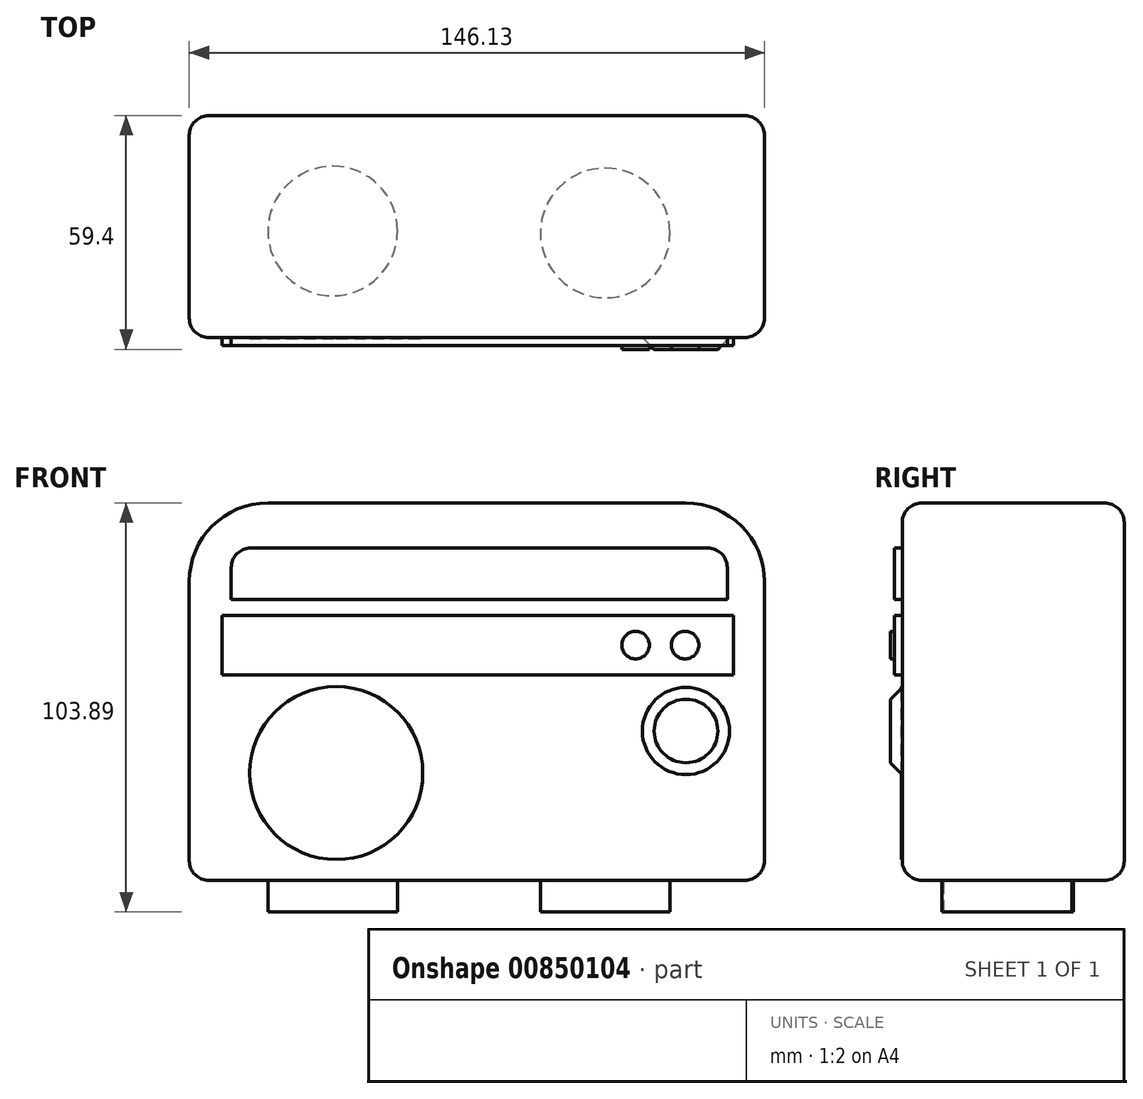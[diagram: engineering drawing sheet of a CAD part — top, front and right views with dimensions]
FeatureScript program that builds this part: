
annotation { "Feature Type Name" : "Feature", "Feature Type Description" : "" }
export const myFeature = defineFeature(function(context is Context, id is Id, definition is map)
    precondition{}
    {
        {
            var Q0;
            Q0=qCreatedBy(makeId("Front.planeOp"),FACE);
            var sketch = newSketch(context, id + "F0", { "sketchPlane" : qUnion([Q0])});
            skLineSegment(sketch, "E0.bottom", {"start": v(-53.18, 52.36) * mm, "end": v(52.95, 52.36) * mm});
            skLineSegment(sketch, "E0.top", {"start": v(-73.18, -43.53) * mm, "end": v(72.95, -43.53) * mm});
            skLineSegment(sketch, "E0.left", {"start": v(-73.18, 32.36) * mm, "end": v(-73.18, -43.53) * mm});
            skLineSegment(sketch, "E0.right", {"start": v(72.95, 32.36) * mm, "end": v(72.95, -43.53) * mm});
            skPoint(sketch, "E1.visualSharp", {"position": v(-73.18, 52.36) * mm});
            skArc(sketch, "E1.filletArc", {"start": v(-53.18, 52.36) * mm, "mid": v(-67.32, 46.5) * mm, "end": v(-73.18, 32.36) * mm});
            skPoint(sketch, "E2.visualSharp", {"position": v(72.95, 52.36) * mm});
            skArc(sketch, "E2.filletArc", {"start": v(72.95, 32.36) * mm, "mid": v(67.09, 46.5) * mm, "end": v(52.95, 52.36) * mm});
            skSolve(sketch);
        }
        {
            var Q0;
            Q0=makeQuery(id+"F0.imprint","IMPRINT",FACE,{"disambiguationData":[TD([[makeQuery(id+"F0.imprint","IMPRINT",EDGE,{"derivedFrom":sQuery(id+"F0.wireOp",EDGE,"E0.bottom")}),-1.0]])]});
            extrude(context, id + "F1", {"entities" : qUnion([Q0]), "oppositeDirection" : true, "depth" : 56.4 * mm, "offsetDistance" : 25 * mm});
        }
        {
            var Q0;
            Q0=makeQuery(id+"F1.opExtrude","SWEPT_FACE",FACE,{"disambiguationData":[OSD([sQuery(id+"F0.wireOp",EDGE,"E0.top")])]});
            var sketch = newSketch(context, id + "F2", { "sketchPlane" : qUnion([Q0])});
            skCircle(sketch, "E3", {"center": v(-36.72, -27.08) * mm, "radius": 16.47 * mm});
            skCircle(sketch, "E4", {"center": v(32.5, -26.61) * mm, "radius": 16.47 * mm});
            skSolve(sketch);
        }
        {
            var Q0;
            Q0=makeQuery(id+"F1.opExtrude","CAP_FACE",FACE,{"disambiguationData":[OSD([sQuery(id+"F0.wireOp",EDGE,"E0.bottom"),sQuery(id+"F0.wireOp",EDGE,"E0.top"),sQuery(id+"F0.wireOp",EDGE,"E0.left"),sQuery(id+"F0.wireOp",EDGE,"E0.right"),sQuery(id+"F0.wireOp",EDGE,"E1.filletArc"),sQuery(id+"F0.wireOp",EDGE,"E2.filletArc")])],"isStart":true});
            var sketch = newSketch(context, id + "F3", { "sketchPlane" : qUnion([Q0])});
            skCircle(sketch, "E5", {"center": v(53.01, -5.58) * mm, "radius": 13.08 * mm});
            skPoint(sketch, "E5.centerSnap0", {"position": v(72.95, -5.58) * mm});
            skSolve(sketch);
        }
        {
            var Q0;
            Q0=makeQuery(id+"F1.opExtrude","CAP_FACE",FACE,{"disambiguationData":[OSD([sQuery(id+"F0.wireOp",EDGE,"E0.bottom"),sQuery(id+"F0.wireOp",EDGE,"E0.top"),sQuery(id+"F0.wireOp",EDGE,"E0.left"),sQuery(id+"F0.wireOp",EDGE,"E0.right"),sQuery(id+"F0.wireOp",EDGE,"E1.filletArc"),sQuery(id+"F0.wireOp",EDGE,"E2.filletArc")])],"isStart":true});
            var sketch = newSketch(context, id + "F4", { "sketchPlane" : qUnion([Q0])});
            skLineSegment(sketch, "E6.bottom", {"start": v(-64.87, 23.84) * mm, "end": v(65.11, 23.84) * mm});
            skLineSegment(sketch, "E6.top", {"start": v(-64.87, 8.66) * mm, "end": v(65.11, 8.66) * mm});
            skLineSegment(sketch, "E6.left", {"start": v(-64.87, 23.84) * mm, "end": v(-64.87, 8.66) * mm});
            skLineSegment(sketch, "E6.right", {"start": v(65.11, 23.84) * mm, "end": v(65.11, 8.66) * mm});
            skSolve(sketch);
        }
        {
            var Q0;
            Q0 = qSketchRegion(id + "F4", true);
            extrude(context, id + "F5", {"entities" : qUnion([Q0]), "depth" : 2 * mm, "offsetDistance" : 25 * mm});
        }
        {
            var Q0;
            Q0=makeQuery(id+"F5.opExtrude","CAP_FACE",FACE,{"disambiguationData":[OSD([sQuery(id+"F4.wireOp",EDGE,"E6.bottom"),sQuery(id+"F4.wireOp",EDGE,"E6.top"),sQuery(id+"F4.wireOp",EDGE,"E6.left"),sQuery(id+"F4.wireOp",EDGE,"E6.right")])],"isStart":false});
            var sketch = newSketch(context, id + "F6", { "sketchPlane" : qUnion([Q0])});
            skCircle(sketch, "E7", {"center": v(52.78, 16.25) * mm, "radius": 3.5 * mm});
            skCircle(sketch, "E8", {"center": v(40.2, 16.25) * mm, "radius": 3.5 * mm});
            skSolve(sketch);
        }
        {
            var Q0;
            Q0 = qSketchRegion(id + "F6", true);
            extrude(context, id + "F7", {"entities" : qUnion([Q0]), "depth" : 1 * mm, "offsetDistance" : 25 * mm});
        }
        {
            var Q0;
            Q0=makeQuery(id+"F2.imprint","IMPRINT",FACE,{"disambiguationData":[TD([[makeQuery(id+"F2.imprint","IMPRINT",EDGE,{"derivedFrom":sQuery(id+"F2.wireOp",EDGE,"E3")}),1.0]])]});
            var Q1;
            Q1=makeQuery(id+"F2.imprint","IMPRINT",FACE,{"disambiguationData":[TD([[makeQuery(id+"F2.imprint","IMPRINT",EDGE,{"derivedFrom":sQuery(id+"F2.wireOp",EDGE,"E4")}),1.0]])]});
            extrude(context, id + "F8", {"entities" : qUnion([Q0, Q1]), "depth" : 8 * mm, "offsetDistance" : 25 * mm});
        }
        {
            var Q0;
            Q0=makeQuery(id+"F3.imprint","IMPRINT",FACE,{"disambiguationData":[TD([[makeQuery(id+"F3.imprint","IMPRINT",EDGE,{"derivedFrom":sQuery(id+"F3.wireOp",EDGE,"E5")}),1.0]])]});
            extrude(context, id + "F9", {"entities" : qUnion([Q0]), "depth" : 3 * mm, "offsetDistance" : 25 * mm});
        }
        {
            var Q0;
            Q0=makeQuery(id+"F1.opExtrude","CAP_FACE",FACE,{"disambiguationData":[OSD([sQuery(id+"F0.wireOp",EDGE,"E0.bottom"),sQuery(id+"F0.wireOp",EDGE,"E0.top"),sQuery(id+"F0.wireOp",EDGE,"E0.left"),sQuery(id+"F0.wireOp",EDGE,"E0.right"),sQuery(id+"F0.wireOp",EDGE,"E1.filletArc"),sQuery(id+"F0.wireOp",EDGE,"E2.filletArc")])],"isStart":true});
            var sketch = newSketch(context, id + "F10", { "sketchPlane" : qUnion([Q0])});
            skLineSegment(sketch, "E9.bottom", {"start": v(-57.5, 40.94) * mm, "end": v(58.5, 40.94) * mm});
            skLineSegment(sketch, "E9.top", {"start": v(-62.5, 27.87) * mm, "end": v(63.5, 27.87) * mm});
            skLineSegment(sketch, "E9.left", {"start": v(-62.5, 35.94) * mm, "end": v(-62.5, 27.87) * mm});
            skLineSegment(sketch, "E9.right", {"start": v(63.5, 35.94) * mm, "end": v(63.5, 27.87) * mm});
            skPoint(sketch, "E10.visualSharp", {"position": v(-62.5, 40.94) * mm});
            skArc(sketch, "E10.filletArc", {"start": v(-57.5, 40.94) * mm, "mid": v(-61.04, 39.47) * mm, "end": v(-62.5, 35.94) * mm});
            skPoint(sketch, "E11.visualSharp", {"position": v(63.5, 40.94) * mm});
            skArc(sketch, "E11.filletArc", {"start": v(63.5, 35.94) * mm, "mid": v(62.03, 39.47) * mm, "end": v(58.5, 40.94) * mm});
            skSolve(sketch);
        }
        {
            var Q0;
            Q0=makeQuery(id+"F10.imprint","IMPRINT",FACE,{"disambiguationData":[TD([[makeQuery(id+"F10.imprint","IMPRINT",EDGE,{"derivedFrom":sQuery(id+"F10.wireOp",EDGE,"E9.bottom")}),-1.0]])]});
            extrude(context, id + "F11", {"entities" : qUnion([Q0]), "depth" : 2 * mm, "offsetDistance" : 25 * mm});
        }
        {
            var Q0;
            Q0=makeQuery(id+"F11.opExtrude","CAP_FACE",FACE,{"disambiguationData":[OSD([sQuery(id+"F10.wireOp",EDGE,"E9.bottom"),sQuery(id+"F10.wireOp",EDGE,"E9.top"),sQuery(id+"F10.wireOp",EDGE,"E9.left"),sQuery(id+"F10.wireOp",EDGE,"E9.right"),sQuery(id+"F10.wireOp",EDGE,"E10.filletArc"),sQuery(id+"F10.wireOp",EDGE,"E11.filletArc")])],"isStart":false});
            var sketch = newSketch(context, id + "F12", { "sketchPlane" : qUnion([Q0])});
            skLineSegment(sketch, "E12", {"start": v(-57.5, 35.94) * mm, "end": v(43.5, 35.94) * mm});
            skLineSegment(sketch, "E13", {"start": v(-56.15, 34.22) * mm, "end": v(44.85, 34.22) * mm});
            skSolve(sketch);
        }
        {
            var Q0;
            Q0=sQuery(id+"F12.wireOp",EDGE,"E13");
            var Q1;
            Q1=sQuery(id+"F12.wireOp",EDGE,"E12");
            extrude(context, id + "F13", {"bodyType" : ToolBodyType.SURFACE, "surfaceEntities" : qUnion([Q0, Q1]), "depth" : 1 * mm, "offsetDistance" : 25 * mm});
        }
        {
            var Q0;
            Q0=makeQuery(id+"F11.opExtrude","CAP_FACE",FACE,{"disambiguationData":[OSD([sQuery(id+"F10.wireOp",EDGE,"E9.bottom"),sQuery(id+"F10.wireOp",EDGE,"E9.top"),sQuery(id+"F10.wireOp",EDGE,"E9.left"),sQuery(id+"F10.wireOp",EDGE,"E9.right"),sQuery(id+"F10.wireOp",EDGE,"E10.filletArc"),sQuery(id+"F10.wireOp",EDGE,"E11.filletArc")])],"isStart":false});
            var sketch = newSketch(context, id + "F14", { "sketchPlane" : qUnion([Q0])});
            skLineSegment(sketch, "E14", {"start": v(-55.64, 31.84) * mm, "end": v(44.36, 31.84) * mm});
            skSolve(sketch);
        }
        {
            var Q0;
            Q0=sQuery(id+"F14.wireOp",EDGE,"E14");
            extrude(context, id + "F15", {"bodyType" : ToolBodyType.SURFACE, "surfaceEntities" : qUnion([Q0]), "depth" : 1 * mm, "offsetDistance" : 25 * mm});
        }
        {
            var Q0;
            Q0=makeQuery(id+"F15.opExtrude","SWEPT_BODY",BODY,{"disambiguationData":[OSD([sQuery(id+"F14.wireOp",EDGE,"E14")])]});
            var Q1;
            Q1=makeQuery(id+"F13.opExtrude","SWEPT_BODY",BODY,{"disambiguationData":[OSD([sQuery(id+"F12.wireOp",EDGE,"E13")])]});
            var Q2;
            Q2=makeQuery(id+"F13.opExtrude","SWEPT_BODY",BODY,{"disambiguationData":[OSD([sQuery(id+"F12.wireOp",EDGE,"E12")])]});
            deleteBodies(context, id + "F16", {"entities" : qUnion([Q0, Q1, Q2])});
        }
        {
            var Q0;
            Q0=makeQuery(id+"F11.opExtrude","CAP_FACE",FACE,{"disambiguationData":[OSD([sQuery(id+"F10.wireOp",EDGE,"E9.bottom"),sQuery(id+"F10.wireOp",EDGE,"E9.top"),sQuery(id+"F10.wireOp",EDGE,"E9.left"),sQuery(id+"F10.wireOp",EDGE,"E9.right"),sQuery(id+"F10.wireOp",EDGE,"E10.filletArc"),sQuery(id+"F10.wireOp",EDGE,"E11.filletArc")])],"isStart":false});
            var sketch = newSketch(context, id + "F17", { "sketchPlane" : qUnion([Q0])});
            skLineSegment(sketch, "E15", {"start": v(-57.5, 35.94) * mm, "end": v(43.64, 35.94) * mm});
            skSolve(sketch);
        }
        {
            var Q0;
            Q0=sQuery(id+"F17.wireOp",EDGE,"E15");
            extrude(context, id + "F18", {"bodyType" : ToolBodyType.SURFACE, "surfaceEntities" : qUnion([Q0]), "depth" : 1 * mm, "offsetDistance" : 25 * mm});
        }
        {
            var Q0;
            Q0=makeQuery(id+"F11.opExtrude","CAP_FACE",FACE,{"disambiguationData":[OSD([sQuery(id+"F10.wireOp",EDGE,"E9.bottom"),sQuery(id+"F10.wireOp",EDGE,"E9.top"),sQuery(id+"F10.wireOp",EDGE,"E9.left"),sQuery(id+"F10.wireOp",EDGE,"E9.right"),sQuery(id+"F10.wireOp",EDGE,"E10.filletArc"),sQuery(id+"F10.wireOp",EDGE,"E11.filletArc")])],"isStart":false});
            var sketch = newSketch(context, id + "F19", { "sketchPlane" : qUnion([Q0])});
            skLineSegment(sketch, "E16", {"start": v(-56.14, 35.4) * mm, "end": v(43.86, 35.4) * mm});
            skSolve(sketch);
        }
        {
            var Q0;
            Q0=sQuery(id+"F19.wireOp",EDGE,"E16");
            extrude(context, id + "F20", {"bodyType" : ToolBodyType.SURFACE, "surfaceEntities" : qUnion([Q0]), "depth" : 1 * mm, "offsetDistance" : 25 * mm});
        }
        {
            var Q0;
            Q0=makeQuery(id+"F11.opExtrude","CAP_FACE",FACE,{"disambiguationData":[OSD([sQuery(id+"F10.wireOp",EDGE,"E9.bottom"),sQuery(id+"F10.wireOp",EDGE,"E9.top"),sQuery(id+"F10.wireOp",EDGE,"E9.left"),sQuery(id+"F10.wireOp",EDGE,"E9.right"),sQuery(id+"F10.wireOp",EDGE,"E10.filletArc"),sQuery(id+"F10.wireOp",EDGE,"E11.filletArc")])],"isStart":false});
            var sketch = newSketch(context, id + "F21", { "sketchPlane" : qUnion([Q0])});
            skLineSegment(sketch, "E17", {"start": v(-57.5, 33.3) * mm, "end": v(42.5, 33.3) * mm});
            skSolve(sketch);
        }
        {
            var Q0;
            Q0=sQuery(id+"F21.wireOp",EDGE,"E17");
            extrude(context, id + "F22", {"bodyType" : ToolBodyType.SURFACE, "surfaceEntities" : qUnion([Q0]), "depth" : 1 * mm, "offsetDistance" : 25 * mm});
        }
        {
            var Q0;
            Q0=makeQuery(id+"F11.opExtrude","CAP_FACE",FACE,{"disambiguationData":[OSD([sQuery(id+"F10.wireOp",EDGE,"E9.bottom"),sQuery(id+"F10.wireOp",EDGE,"E9.top"),sQuery(id+"F10.wireOp",EDGE,"E9.left"),sQuery(id+"F10.wireOp",EDGE,"E9.right"),sQuery(id+"F10.wireOp",EDGE,"E10.filletArc"),sQuery(id+"F10.wireOp",EDGE,"E11.filletArc")])],"isStart":false});
            var sketch = newSketch(context, id + "F23", { "sketchPlane" : qUnion([Q0])});
            skLineSegment(sketch, "E18", {"start": v(-56.14, 31.84) * mm, "end": v(44.23, 31.84) * mm});
            skSolve(sketch);
        }
        {
            var Q0;
            Q0=sQuery(id+"F23.wireOp",EDGE,"E18");
            extrude(context, id + "F24", {"bodyType" : ToolBodyType.SURFACE, "surfaceEntities" : qUnion([Q0]), "depth" : 1 * mm, "offsetDistance" : 25 * mm});
        }
        {
            var Q0;
            Q0=makeQuery(id+"F11.opExtrude","CAP_FACE",FACE,{"disambiguationData":[OSD([sQuery(id+"F10.wireOp",EDGE,"E9.bottom"),sQuery(id+"F10.wireOp",EDGE,"E9.top"),sQuery(id+"F10.wireOp",EDGE,"E9.left"),sQuery(id+"F10.wireOp",EDGE,"E9.right"),sQuery(id+"F10.wireOp",EDGE,"E10.filletArc"),sQuery(id+"F10.wireOp",EDGE,"E11.filletArc")])],"isStart":false});
            var sketch = newSketch(context, id + "F25", { "sketchPlane" : qUnion([Q0])});
            skLineSegment(sketch, "E19", {"start": v(-56.14, 30.25) * mm, "end": v(43.86, 30.25) * mm});
            skSolve(sketch);
        }
        {
            var Q0;
            Q0=sQuery(id+"F25.wireOp",EDGE,"E19");
            extrude(context, id + "F26", {"bodyType" : ToolBodyType.SURFACE, "surfaceEntities" : qUnion([Q0]), "depth" : 1 * mm, "offsetDistance" : 25 * mm});
        }
        {
            var Q0;
            Q0=makeQuery(id+"F11.opExtrude","CAP_FACE",FACE,{"disambiguationData":[OSD([sQuery(id+"F10.wireOp",EDGE,"E9.bottom"),sQuery(id+"F10.wireOp",EDGE,"E9.top"),sQuery(id+"F10.wireOp",EDGE,"E9.left"),sQuery(id+"F10.wireOp",EDGE,"E9.right"),sQuery(id+"F10.wireOp",EDGE,"E10.filletArc"),sQuery(id+"F10.wireOp",EDGE,"E11.filletArc")])],"isStart":false});
            var sketch = newSketch(context, id + "F27", { "sketchPlane" : qUnion([Q0])});
            skLineSegment(sketch, "E20", {"start": v(-55.94, 39.18) * mm, "end": v(44.06, 39.18) * mm});
            skSolve(sketch);
        }
        {
            var Q0;
            Q0=sQuery(id+"F27.wireOp",EDGE,"E20");
            extrude(context, id + "F28", {"bodyType" : ToolBodyType.SURFACE, "surfaceEntities" : qUnion([Q0]), "depth" : 1 * mm, "offsetDistance" : 25 * mm});
        }
        {
            var Q0;
            Q0=makeQuery(id+"F9.opExtrude","CAP_FACE",FACE,{"disambiguationData":[OSD([sQuery(id+"F3.wireOp",EDGE,"E5")])],"isStart":false});
            chamfer(context, id + "F29", {"entities" : qUnion([Q0]), "width" : 5 * mm, "tangentPropagation" : true});
        }
        {
            var Q0;
            Q0=makeQuery(id+"F11.opExtrude","CAP_FACE",FACE,{"disambiguationData":[OSD([sQuery(id+"F10.wireOp",EDGE,"E9.bottom"),sQuery(id+"F10.wireOp",EDGE,"E9.top"),sQuery(id+"F10.wireOp",EDGE,"E9.left"),sQuery(id+"F10.wireOp",EDGE,"E9.right"),sQuery(id+"F10.wireOp",EDGE,"E10.filletArc"),sQuery(id+"F10.wireOp",EDGE,"E11.filletArc")])],"isStart":false});
            var sketch = newSketch(context, id + "F30", { "sketchPlane" : qUnion([Q0])});
            skLineSegment(sketch, "E21", {"start": v(43.64, 40.94) * mm, "end": v(43.64, 27.87) * mm});
            skSolve(sketch);
        }
        {
            var Q0;
            Q0=sQuery(id+"F30.wireOp",EDGE,"E21");
            extrude(context, id + "F31", {"bodyType" : ToolBodyType.SURFACE, "surfaceEntities" : qUnion([Q0]), "depth" : 1 * mm, "offsetDistance" : 25 * mm});
        }
        {
            var Q0;
            Q0=makeQuery(id+"F11.opExtrude","CAP_FACE",FACE,{"disambiguationData":[OSD([sQuery(id+"F10.wireOp",EDGE,"E9.bottom"),sQuery(id+"F10.wireOp",EDGE,"E9.top"),sQuery(id+"F10.wireOp",EDGE,"E9.left"),sQuery(id+"F10.wireOp",EDGE,"E9.right"),sQuery(id+"F10.wireOp",EDGE,"E10.filletArc"),sQuery(id+"F10.wireOp",EDGE,"E11.filletArc")])],"isStart":false});
            var sketch = newSketch(context, id + "F32", { "sketchPlane" : qUnion([Q0])});
            skLineSegment(sketch, "E22", {"start": v(-57.5, 40.94) * mm, "end": v(-57.5, 27.87) * mm});
            skSolve(sketch);
        }
        {
            var Q0;
            Q0=sQuery(id+"F32.wireOp",EDGE,"E22");
            extrude(context, id + "F33", {"bodyType" : ToolBodyType.SURFACE, "surfaceEntities" : qUnion([Q0]), "depth" : 1 * mm, "offsetDistance" : 25 * mm});
        }
        {
            var Q0;
            Q0=makeQuery(id+"F1.opExtrude","CAP_FACE",FACE,{"disambiguationData":[OSD([sQuery(id+"F0.wireOp",EDGE,"E0.bottom"),sQuery(id+"F0.wireOp",EDGE,"E0.top"),sQuery(id+"F0.wireOp",EDGE,"E0.left"),sQuery(id+"F0.wireOp",EDGE,"E0.right"),sQuery(id+"F0.wireOp",EDGE,"E1.filletArc"),sQuery(id+"F0.wireOp",EDGE,"E2.filletArc")])],"isStart":true});
            fillet(context, id + "F34", {"entities" : qUnion([Q0]), "radius" : 5 * mm, "tangentPropagation" : true, "allowEdgeOverflow" : false});
        }
        {
            var Q0;
            Q0=makeQuery(id+"F1.opExtrude","CAP_FACE",FACE,{"disambiguationData":[OSD([sQuery(id+"F0.wireOp",EDGE,"E0.bottom"),sQuery(id+"F0.wireOp",EDGE,"E0.top"),sQuery(id+"F0.wireOp",EDGE,"E0.left"),sQuery(id+"F0.wireOp",EDGE,"E0.right"),sQuery(id+"F0.wireOp",EDGE,"E1.filletArc"),sQuery(id+"F0.wireOp",EDGE,"E2.filletArc")])],"isStart":false});
            fillet(context, id + "F35", {"entities" : qUnion([Q0]), "radius" : 5 * mm, "tangentPropagation" : true, "allowEdgeOverflow" : false});
        }
        {
            var Q0;
            Q0=makeQuery(id+"F1.opExtrude","SWEPT_FACE",FACE,{"disambiguationData":[OSD([sQuery(id+"F0.wireOp",EDGE,"E0.right")])]});
            fillet(context, id + "F36", {"entities" : qUnion([Q0]), "radius" : 5 * mm, "tangentPropagation" : true, "allowEdgeOverflow" : false});
        }
        {
            var Q0;
            Q0=makeQuery(id+"F1.opExtrude","SWEPT_FACE",FACE,{"disambiguationData":[OSD([sQuery(id+"F0.wireOp",EDGE,"E0.left")])]});
            fillet(context, id + "F37", {"entities" : qUnion([Q0]), "radius" : 5 * mm, "tangentPropagation" : true, "allowEdgeOverflow" : false});
        }
        {
            var Q0;
            Q0=makeQuery(id+"F18.opExtrude","SWEPT_BODY",BODY,{"disambiguationData":[OSD([sQuery(id+"F17.wireOp",EDGE,"E15")])]});
            var Q1;
            Q1=makeQuery(id+"F28.opExtrude","SWEPT_BODY",BODY,{"disambiguationData":[OSD([sQuery(id+"F27.wireOp",EDGE,"E20")])]});
            var Q2;
            Q2=makeQuery(id+"F22.opExtrude","SWEPT_BODY",BODY,{"disambiguationData":[OSD([sQuery(id+"F21.wireOp",EDGE,"E17")])]});
            var Q3;
            Q3=makeQuery(id+"F26.opExtrude","SWEPT_BODY",BODY,{"disambiguationData":[OSD([sQuery(id+"F25.wireOp",EDGE,"E19")])]});
            var Q4;
            Q4=makeQuery(id+"F24.opExtrude","SWEPT_BODY",BODY,{"disambiguationData":[OSD([sQuery(id+"F23.wireOp",EDGE,"E18")])]});
            deleteBodies(context, id + "F38", {"entities" : qUnion([Q0, Q1, Q2, Q3, Q4])});
        }
        {
            var Q0;
            Q0=makeQuery(id+"F20.opExtrude","SWEPT_BODY",BODY,{"disambiguationData":[OSD([sQuery(id+"F19.wireOp",EDGE,"E16")])]});
            deleteBodies(context, id + "F39", {"entities" : qUnion([Q0])});
        }
        {
            var Q0;
            Q0=makeQuery(id+"F1.opExtrude","CAP_FACE",FACE,{"disambiguationData":[OSD([sQuery(id+"F0.wireOp",EDGE,"E0.bottom"),sQuery(id+"F0.wireOp",EDGE,"E0.top"),sQuery(id+"F0.wireOp",EDGE,"E0.left"),sQuery(id+"F0.wireOp",EDGE,"E0.right"),sQuery(id+"F0.wireOp",EDGE,"E1.filletArc"),sQuery(id+"F0.wireOp",EDGE,"E2.filletArc")])],"isStart":true});
            var sketch = newSketch(context, id + "F40", { "sketchPlane" : qUnion([Q0])});
            skCircle(sketch, "E23", {"center": v(-35.84, -16.26) * mm, "radius": 22 * mm});
            skSolve(sketch);
        }
        {
            var Q0;
            Q0=makeQuery(id+"F40.imprint","IMPRINT",FACE,{"disambiguationData":[TD([[makeQuery(id+"F40.imprint","IMPRINT",EDGE,{"derivedFrom":sQuery(id+"F40.wireOp",EDGE,"E23")}),1.0]])]});
            extrude(context, id + "F41", {"entities" : qUnion([Q0]), "depth" : 0.2 * mm, "offsetDistance" : 25 * mm});
        }
        {
            var Q0;
            Q0=makeQuery(id+"F41.opExtrude","CAP_FACE",FACE,{"disambiguationData":[OSD([sQuery(id+"F40.wireOp",EDGE,"E23")])],"isStart":false});
            var sketch = newSketch(context, id + "F42", { "sketchPlane" : qUnion([Q0])});
            skLineSegment(sketch, "E24", {"start": v(-50.66, 0) * mm, "end": v(-21.02, 0) * mm});
            skLineSegment(sketch, "E25", {"start": v(-52.31, -1.68) * mm, "end": v(-19.37, -1.68) * mm});
            skLineSegment(sketch, "E26", {"start": v(-53.38, -2.99) * mm, "end": v(-18.3, -2.99) * mm});
            skLineSegment(sketch, "E27", {"start": v(-54.36, -4.39) * mm, "end": v(-17.32, -4.39) * mm});
            skLineSegment(sketch, "E28", {"start": v(-54.87, -5.23) * mm, "end": v(-16.8, -5.23) * mm});
            skLineSegment(sketch, "E29", {"start": v(-55.58, -6.55) * mm, "end": v(-16.1, -6.55) * mm});
            skLineSegment(sketch, "E30", {"start": v(-56.12, -7.74) * mm, "end": v(-15.56, -7.74) * mm});
            skLineSegment(sketch, "E31", {"start": v(-51.49, -0.8) * mm, "end": v(-20.2, -0.8) * mm});
            skLineSegment(sketch, "E32", {"start": v(-56.58, -8.92) * mm, "end": v(-15.1, -8.92) * mm});
            skLineSegment(sketch, "E33", {"start": v(-56.98, -10.18) * mm, "end": v(-14.7, -10.18) * mm});
            skLineSegment(sketch, "E34", {"start": v(-57.27, -11.27) * mm, "end": v(-14.42, -11.27) * mm});
            skLineSegment(sketch, "E35", {"start": v(-57.5, -12.41) * mm, "end": v(-14.18, -12.41) * mm});
            skLineSegment(sketch, "E36", {"start": v(-57.66, -13.44) * mm, "end": v(-14.03, -13.44) * mm});
            skLineSegment(sketch, "E37", {"start": v(-57.77, -14.46) * mm, "end": v(-13.92, -14.46) * mm});
            skLineSegment(sketch, "E38", {"start": v(-57.83, -15.54) * mm, "end": v(-13.86, -15.54) * mm});
            skLineSegment(sketch, "E39", {"start": v(-57.84, -16.53) * mm, "end": v(-13.85, -16.53) * mm});
            skLineSegment(sketch, "E40", {"start": v(-57.8, -17.6) * mm, "end": v(-13.89, -17.6) * mm});
            skLineSegment(sketch, "E41", {"start": v(-57.73, -18.46) * mm, "end": v(-13.96, -18.46) * mm});
            skLineSegment(sketch, "E42", {"start": v(-57.59, -19.57) * mm, "end": v(-14.1, -19.57) * mm});
            skLineSegment(sketch, "E43", {"start": v(-57.39, -20.7) * mm, "end": v(-14.3, -20.7) * mm});
            skLineSegment(sketch, "E44", {"start": v(-57.16, -21.67) * mm, "end": v(-14.52, -21.67) * mm});
            skLineSegment(sketch, "E45", {"start": v(-56.94, -22.47) * mm, "end": v(-14.74, -22.47) * mm});
            skLineSegment(sketch, "E46", {"start": v(-56.65, -23.4) * mm, "end": v(-15.04, -23.4) * mm});
            skLineSegment(sketch, "E47", {"start": v(-56.27, -24.42) * mm, "end": v(-15.41, -24.42) * mm});
            skLineSegment(sketch, "E48", {"start": v(-55.87, -25.35) * mm, "end": v(-15.81, -25.35) * mm});
            skLineSegment(sketch, "E49", {"start": v(-55.31, -26.5) * mm, "end": v(-16.37, -26.5) * mm});
            skLineSegment(sketch, "E50", {"start": v(-54.73, -27.53) * mm, "end": v(-16.95, -27.53) * mm});
            skLineSegment(sketch, "E51", {"start": v(-54.3, -28.22) * mm, "end": v(-17.38, -28.22) * mm});
            skLineSegment(sketch, "E52", {"start": v(-53.66, -29.16) * mm, "end": v(-18.02, -29.16) * mm});
            skLineSegment(sketch, "E53", {"start": v(-52.8, -30.26) * mm, "end": v(-18.87, -30.26) * mm});
            skLineSegment(sketch, "E54", {"start": v(-52.04, -31.15) * mm, "end": v(-19.65, -31.15) * mm});
            skLineSegment(sketch, "E55", {"start": v(-51.3, -31.91) * mm, "end": v(-20.39, -31.91) * mm});
            skLineSegment(sketch, "E56", {"start": v(-50.38, -32.76) * mm, "end": v(-21.3, -32.76) * mm});
            skLineSegment(sketch, "E57", {"start": v(-49.41, -33.57) * mm, "end": v(-22.27, -33.57) * mm});
            skLineSegment(sketch, "E58", {"start": v(-48.63, -34.16) * mm, "end": v(-23.05, -34.16) * mm});
            skLineSegment(sketch, "E59", {"start": v(-47.54, -34.89) * mm, "end": v(-24.14, -34.89) * mm});
            skLineSegment(sketch, "E60", {"start": v(-46.14, -35.7) * mm, "end": v(-25.54, -35.7) * mm});
            skLineSegment(sketch, "E61", {"start": v(-43.41, -36.91) * mm, "end": v(-27.31, -36.53) * mm});
            skLineSegment(sketch, "E62", {"start": v(-40.68, -37.72) * mm, "end": v(-31, -37.72) * mm});
            skLineSegment(sketch, "E63", {"start": v(-49.69, 0.83) * mm, "end": v(-22, 0.83) * mm});
            skLineSegment(sketch, "E64", {"start": v(-48.31, 1.86) * mm, "end": v(-23.37, 1.86) * mm});
            skLineSegment(sketch, "E65", {"start": v(-46.57, 2.94) * mm, "end": v(-25.11, 2.94) * mm});
            skLineSegment(sketch, "E66", {"start": v(-44.42, 4) * mm, "end": v(-27.26, 4) * mm});
            skLineSegment(sketch, "E67", {"start": v(-41.86, 4.9) * mm, "end": v(-29.82, 4.9) * mm});
            skSolve(sketch);
        }
        {
            var Q0;
            Q0=sQuery(id+"F42.wireOp",EDGE,"E67");
            var Q1;
            Q1=sQuery(id+"F42.wireOp",EDGE,"E66");
            var Q2;
            Q2=sQuery(id+"F42.wireOp",EDGE,"E65");
            var Q3;
            Q3=sQuery(id+"F42.wireOp",EDGE,"E64");
            var Q4;
            Q4=sQuery(id+"F42.wireOp",EDGE,"E63");
            var Q5;
            Q5=sQuery(id+"F42.wireOp",EDGE,"E24");
            var Q6;
            Q6=sQuery(id+"F42.wireOp",EDGE,"E31");
            var Q7;
            Q7=sQuery(id+"F42.wireOp",EDGE,"E25");
            var Q8;
            Q8=sQuery(id+"F42.wireOp",EDGE,"E26");
            var Q9;
            Q9=sQuery(id+"F42.wireOp",EDGE,"E27");
            var Q10;
            Q10=sQuery(id+"F42.wireOp",EDGE,"E28");
            var Q11;
            Q11=sQuery(id+"F42.wireOp",EDGE,"E29");
            var Q12;
            Q12=sQuery(id+"F42.wireOp",EDGE,"E30");
            var Q13;
            Q13=sQuery(id+"F42.wireOp",EDGE,"E32");
            var Q14;
            Q14=sQuery(id+"F42.wireOp",EDGE,"E33");
            var Q15;
            Q15=sQuery(id+"F42.wireOp",EDGE,"E34");
            var Q16;
            Q16=sQuery(id+"F42.wireOp",EDGE,"E35");
            var Q17;
            Q17=sQuery(id+"F42.wireOp",EDGE,"E36");
            var Q18;
            Q18=sQuery(id+"F42.wireOp",EDGE,"E37");
            var Q19;
            Q19=sQuery(id+"F42.wireOp",EDGE,"E38");
            var Q20;
            Q20=sQuery(id+"F42.wireOp",EDGE,"E39");
            var Q21;
            Q21=sQuery(id+"F42.wireOp",EDGE,"E40");
            var Q22;
            Q22=sQuery(id+"F42.wireOp",EDGE,"E41");
            var Q23;
            Q23=sQuery(id+"F42.wireOp",EDGE,"E42");
            var Q24;
            Q24=sQuery(id+"F42.wireOp",EDGE,"E43");
            var Q25;
            Q25=sQuery(id+"F42.wireOp",EDGE,"E44");
            var Q26;
            Q26=sQuery(id+"F42.wireOp",EDGE,"E45");
            var Q27;
            Q27=sQuery(id+"F42.wireOp",EDGE,"E46");
            var Q28;
            Q28=sQuery(id+"F42.wireOp",EDGE,"E47");
            var Q29;
            Q29=sQuery(id+"F42.wireOp",EDGE,"E48");
            var Q30;
            Q30=sQuery(id+"F42.wireOp",EDGE,"E49");
            var Q31;
            Q31=sQuery(id+"F42.wireOp",EDGE,"E50");
            var Q32;
            Q32=sQuery(id+"F42.wireOp",EDGE,"E51");
            var Q33;
            Q33=sQuery(id+"F42.wireOp",EDGE,"E52");
            var Q34;
            Q34=sQuery(id+"F42.wireOp",EDGE,"E53");
            var Q35;
            Q35=sQuery(id+"F42.wireOp",EDGE,"E54");
            var Q36;
            Q36=sQuery(id+"F42.wireOp",EDGE,"E55");
            var Q37;
            Q37=sQuery(id+"F42.wireOp",EDGE,"E56");
            var Q38;
            Q38=sQuery(id+"F42.wireOp",EDGE,"E58");
            var Q39;
            Q39=sQuery(id+"F42.wireOp",EDGE,"E57");
            var Q40;
            Q40=sQuery(id+"F42.wireOp",EDGE,"E59");
            var Q41;
            Q41=sQuery(id+"F42.wireOp",EDGE,"E60");
            var Q42;
            Q42=sQuery(id+"F42.wireOp",EDGE,"E61");
            var Q43;
            Q43=sQuery(id+"F42.wireOp",EDGE,"E62");
            extrude(context, id + "F43", {"bodyType" : ToolBodyType.SURFACE, "surfaceEntities" : qUnion([Q0, Q1, Q2, Q3, Q4, Q5, Q6, Q7, Q8, Q9, Q10, Q11, Q12, Q13, Q14, Q15, Q16, Q17, Q18, Q19, Q20, Q21, Q22, Q23, Q24, Q25, Q26, Q27, Q28, Q29, Q30, Q31, Q32, Q33, Q34, Q35, Q36, Q37, Q38, Q39, Q40, Q41, Q42, Q43]), "depth" : 1 * mm, "offsetDistance" : 25 * mm});
        }
    });
